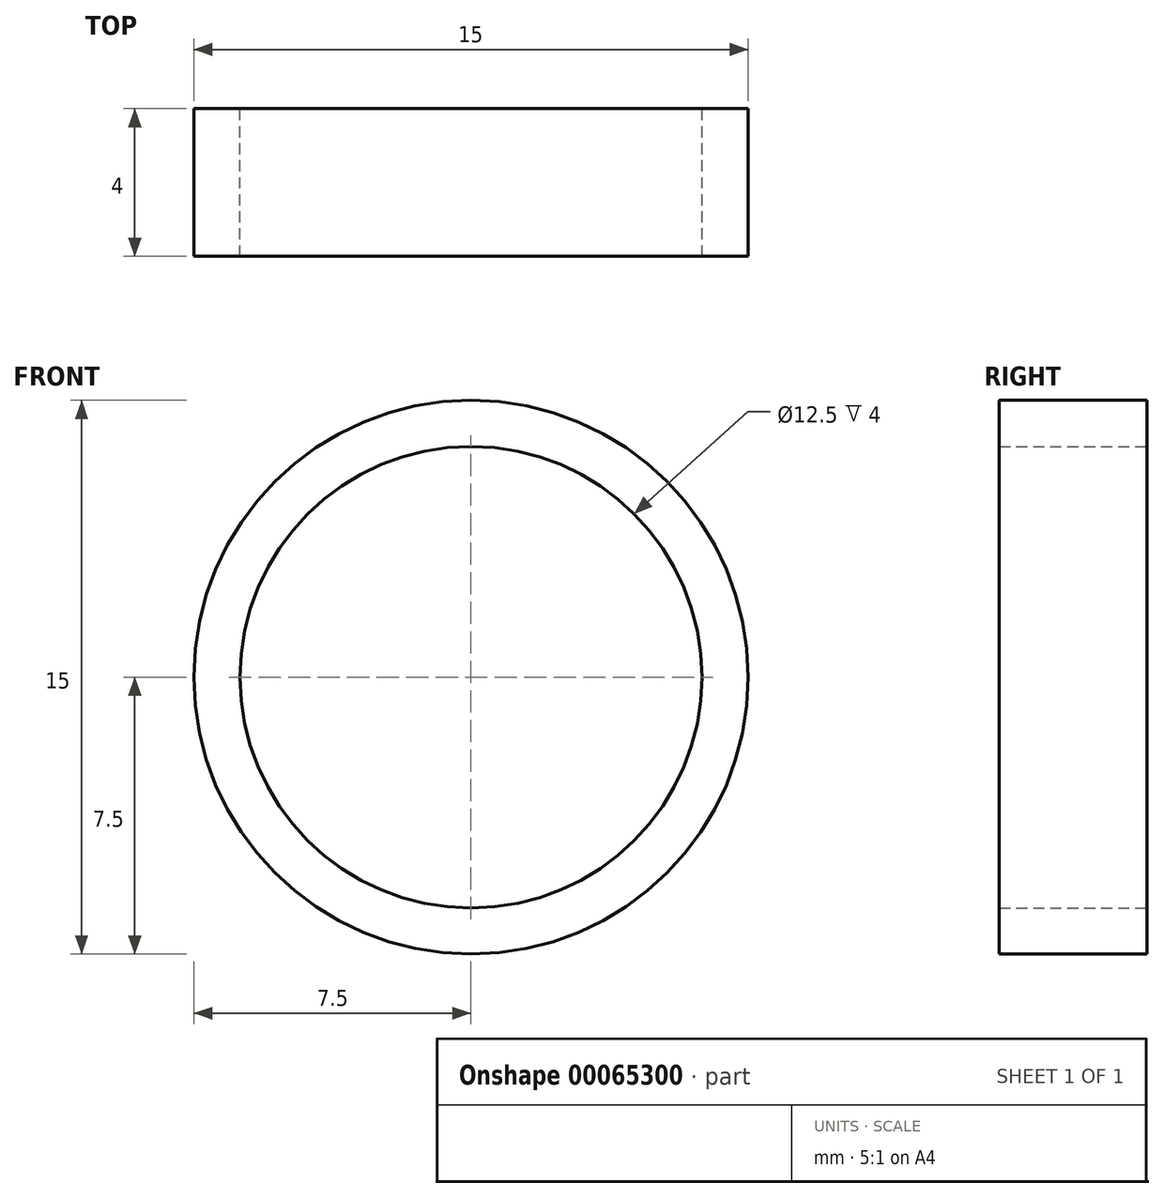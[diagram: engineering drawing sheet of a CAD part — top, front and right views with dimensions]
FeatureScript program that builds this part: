
annotation { "Feature Type Name" : "Feature", "Feature Type Description" : "" }
export const myFeature = defineFeature(function(context is Context, id is Id, definition is map)
    precondition{}
    {
        {
            var Q0;
            Q0=qCreatedBy(makeId("Front.planeOp"),FACE);
            var sketch = newSketch(context, id + "F0", { "sketchPlane" : qUnion([Q0])});
            skCircle(sketch, "E0", {"center": v(0, 0) * mm, "radius": 7.5 * mm});
            skCircle(sketch, "E1", {"center": v(0, 0) * mm, "radius": 6.25 * mm});
            skSolve(sketch);
        }
        {
            var Q0;
            Q0=makeQuery(id+"F0.imprint","IMPRINT",FACE,{"disambiguationData":[TD([[makeQuery(id+"F0.imprint","IMPRINT",EDGE,{"derivedFrom":sQuery(id+"F0.wireOp",EDGE,"E0")}),1.0]])]});
            extrude(context, id + "F1", {"entities" : qUnion([Q0]), "depth" : 4 * mm});
        }
    });
